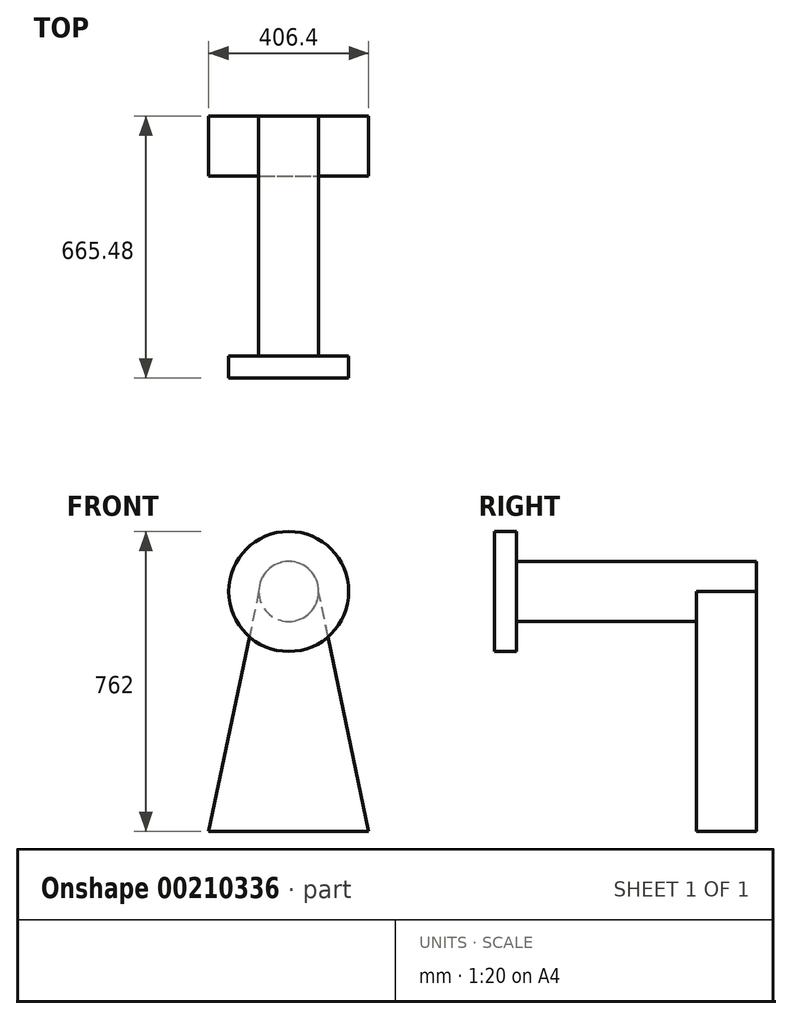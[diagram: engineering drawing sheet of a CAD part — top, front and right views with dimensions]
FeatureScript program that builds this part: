
annotation { "Feature Type Name" : "Feature", "Feature Type Description" : "" }
export const myFeature = defineFeature(function(context is Context, id is Id, definition is map)
    precondition{}
    {
        {
            var Q0;
            Q0=qCreatedBy(makeId("Front.planeOp"),FACE);
            var sketch = newSketch(context, id + "F0", { "sketchPlane" : qUnion([Q0])});
            skCircle(sketch, "E0", {"center": v(0, 0) * mm, "radius": 76.2 * mm});
            skLineSegment(sketch, "E1", {"start": v(-76.2, 0) * mm, "end": v(-203.2, -609.6) * mm});
            skLineSegment(sketch, "E2", {"start": v(-203.2, -609.6) * mm, "end": v(203.2, -609.6) * mm});
            skLineSegment(sketch, "E3", {"start": v(203.2, -609.6) * mm, "end": v(76.2, 0) * mm});
            skSolve(sketch);
        }
        {
            var Q0;
            {var subQ0=sQuery(id+"F0.wireOp",EDGE,"E0");var subQ1=makeQuery(id+"F0.imprint","INTERSECT",VERTEX,{"derivedFrom":[subQ0,sQuery(id+"F0.wireOp",EDGE,"E1")]});Q0=makeQuery(id+"F0.imprint","IMPRINT",FACE,{"disambiguationData":[TD([[makeQuery(id+"F0.imprint","IMPRINT",EDGE,{"disambiguationData":[TD([[subQ1,1.0]])],"derivedFrom":subQ0}),1.0]])]});}
            extrude(context, id + "F1", {"entities" : qUnion([Q0]), "depth" : 609.6 * mm});
        }
        {
            var Q0;
            {var subQ0=sQuery(id+"F0.wireOp",EDGE,"E1");Q0=makeQuery(id+"F0.imprint","IMPRINT",FACE,{"disambiguationData":[TD([[makeQuery(id+"F0.imprint","IMPRINT",EDGE,{"derivedFrom":subQ0}),1.0]])]});}
            extrude(context, id + "F2", {"entities" : qUnion([Q0]), "operationType" : NewBodyOperationType.ADD, "depth" : 152.4 * mm});
        }
        {
            var Q0;
            Q0=makeQuery(id+"F1.opExtrude","CAP_FACE",FACE,{"disambiguationData":[OSD([sQuery(id+"F0.wireOp",EDGE,"E0")])],"isStart":false});
            var sketch = newSketch(context, id + "F3", { "sketchPlane" : qUnion([Q0])});
            skCircle(sketch, "E4", {"center": v(0, 0) * mm, "radius": 152.4 * mm});
            skSolve(sketch);
        }
        {
            var Q0;
            Q0 = qSketchRegion(id + "F3", true);
            extrude(context, id + "F4", {"entities" : qUnion([Q0]), "operationType" : NewBodyOperationType.ADD, "depth" : 55.88 * mm});
        }
    });
